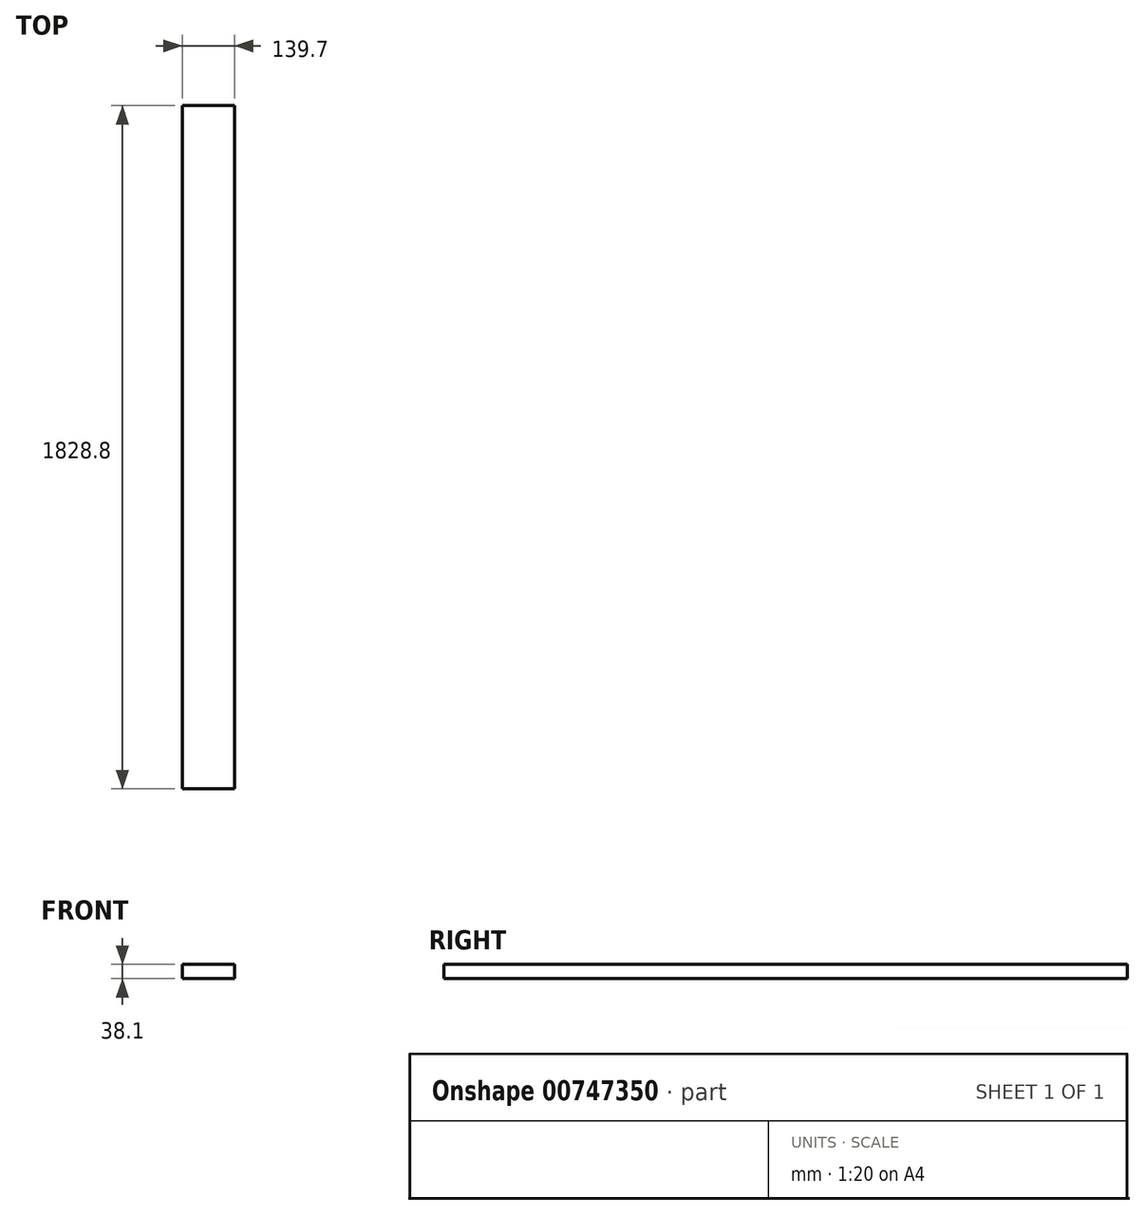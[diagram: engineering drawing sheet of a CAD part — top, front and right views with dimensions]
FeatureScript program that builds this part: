
annotation { "Feature Type Name" : "Feature", "Feature Type Description" : "" }
export const myFeature = defineFeature(function(context is Context, id is Id, definition is map)
    precondition{}
    {
        {
            var Q0;
            Q0=qCreatedBy(makeId("Front.planeOp"),FACE);
            var sketch = newSketch(context, id + "F0", { "sketchPlane" : qUnion([Q0])});
            skLineSegment(sketch, "E0.bottom", {"start": v(0, 0) * mm, "end": v(139.7, 0) * mm});
            skLineSegment(sketch, "E0.top", {"start": v(0, 38.1) * mm, "end": v(139.7, 38.1) * mm});
            skLineSegment(sketch, "E0.left", {"start": v(0, 0) * mm, "end": v(0, 38.1) * mm});
            skLineSegment(sketch, "E0.right", {"start": v(139.7, 0) * mm, "end": v(139.7, 38.1) * mm});
            skSolve(sketch);
        }
        {
            var Q0;
            Q0=qSketchRegion(id+"F0",true);
            extrude(context, id + "F1", {"entities" : qUnion([Q0]), "depth" : 1828.8 * mm, "offsetDistance" : 25.4 * mm});
        }
    });
